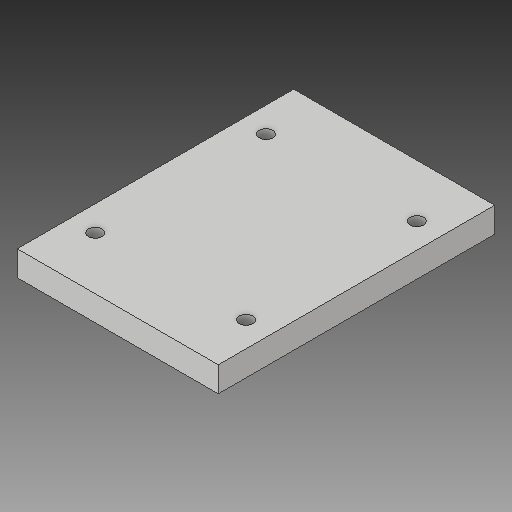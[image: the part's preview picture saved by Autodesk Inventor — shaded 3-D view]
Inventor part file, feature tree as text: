
AUTODESK INVENTOR PART (.ipt)
format: ipt  version: 2019 (Build 230136000, 136)  size: 104,960 bytes
history: native  units: mm
features: extrude x2, sketch x2
ambient origin geometry x8: Origin, YZ Plane, XZ Plane, XY Plane, X Axis, Y Axis, Z Axis, Center Point
bodies: Solid1 (feature_tree)
feature tree (4):
  extrude  "Extrusion1"  Depth=55.0mm
  extrude  "Extrusion2"  Depth=5.0mm
  sketch  "Sketch1"  dims[d0=40.0mm d1=55.0mm]
  sketch  "Sketch2"  dims[d2=2.7mm d3=2.7mm d4=2.7mm d5=2.7mm d6=5.0mm d7=0.0mm d8=11.0mm d9=5.0mm d10=0.0mm]
